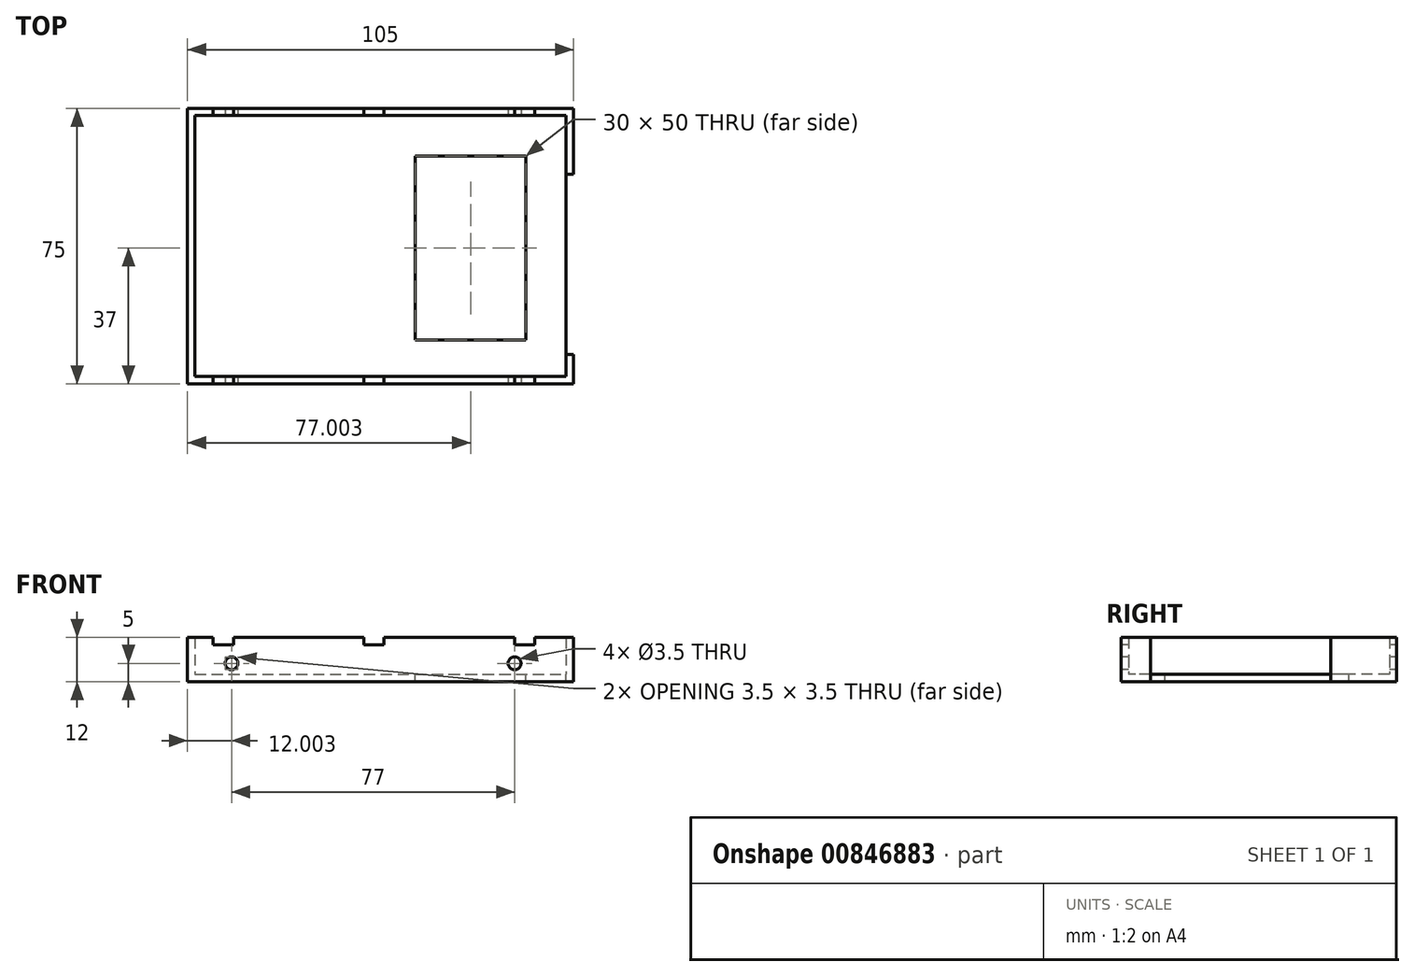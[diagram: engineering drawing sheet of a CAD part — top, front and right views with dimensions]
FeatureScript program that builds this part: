
annotation { "Feature Type Name" : "Feature", "Feature Type Description" : "" }
export const myFeature = defineFeature(function(context is Context, id is Id, definition is map)
    precondition{}
    {
        {
            var Q0;
            Q0=qCreatedBy(makeId("Top.planeOp"),FACE);
            var sketch = newSketch(context, id + "F0", { "sketchPlane" : qUnion([Q0])});
            skLineSegment(sketch, "E0.bottom", {"start": v(-42.38, 29.9) * mm, "end": v(58.62, 29.9) * mm});
            skLineSegment(sketch, "E0.top", {"start": v(-42.38, -41.1) * mm, "end": v(58.62, -41.1) * mm});
            skLineSegment(sketch, "E0.left", {"start": v(-42.38, 29.9) * mm, "end": v(-42.38, -41.1) * mm});
            skLineSegment(sketch, "E0.right", {"start": v(58.62, 29.9) * mm, "end": v(58.62, -41.1) * mm});
            skLineSegment(sketch, "E1.left", {"start": v(-42.38, 29.9) * mm, "end": v(-42.38, 29.9) * mm});
            skLineSegment(sketch, "E1.right", {"start": v(58.62, 29.9) * mm, "end": v(58.62, 29.9) * mm});
            skLineSegment(sketch, "E2.top", {"start": v(-42.38, 31.9) * mm, "end": v(58.62, 31.9) * mm});
            skLineSegment(sketch, "E2.left", {"start": v(-42.38, 29.9) * mm, "end": v(-42.38, 31.9) * mm});
            skLineSegment(sketch, "E2.right", {"start": v(58.62, 29.9) * mm, "end": v(58.62, 31.9) * mm});
            skLineSegment(sketch, "E3.top", {"start": v(-42.38, -43.1) * mm, "end": v(58.62, -43.1) * mm});
            skLineSegment(sketch, "E3.left", {"start": v(-42.38, -41.1) * mm, "end": v(-42.38, -43.1) * mm});
            skLineSegment(sketch, "E3.right", {"start": v(58.62, -41.1) * mm, "end": v(58.62, -43.1) * mm});
            skLineSegment(sketch, "E4.bottom", {"start": v(-42.38, 31.9) * mm, "end": v(-44.38, 31.9) * mm});
            skLineSegment(sketch, "E4.top", {"start": v(-42.38, -43.1) * mm, "end": v(-44.38, -43.1) * mm});
            skLineSegment(sketch, "E4.left", {"start": v(-42.38, 31.9) * mm, "end": v(-42.38, -43.1) * mm});
            skLineSegment(sketch, "E4.right", {"start": v(-44.38, 31.9) * mm, "end": v(-44.38, -43.1) * mm});
            skLineSegment(sketch, "E5.bottom", {"start": v(58.62, 31.9) * mm, "end": v(60.62, 31.9) * mm});
            skLineSegment(sketch, "E5.top", {"start": v(58.62, -43.1) * mm, "end": v(60.62, -43.1) * mm});
            skLineSegment(sketch, "E5.left", {"start": v(58.62, 31.9) * mm, "end": v(58.62, -43.1) * mm});
            skLineSegment(sketch, "E5.right", {"start": v(60.62, 31.9) * mm, "end": v(60.62, -43.1) * mm});
            skSolve(sketch);
        }
        {
            var Q0;
            {var subQ3=sQuery(id+"F0.wireOp",EDGE,"E4.bottom");Q0=makeQuery(id+"F0.imprint","IMPRINT",FACE,{"disambiguationData":[TD([[makeQuery(id+"F0.imprint","IMPRINT",EDGE,{"derivedFrom":subQ3}),1.0]])]});}
            var Q1;
            {var subQ0=sQuery(id+"F0.wireOp",EDGE,"E0.bottom");Q1=makeQuery(id+"F0.imprint","IMPRINT",FACE,{"disambiguationData":[TD([[makeQuery(id+"F0.imprint","IMPRINT",EDGE,{"derivedFrom":subQ0}),1.0]])]});}
            var Q2;
            {var subQ3=sQuery(id+"F0.wireOp",EDGE,"E5.bottom");Q2=makeQuery(id+"F0.imprint","IMPRINT",FACE,{"disambiguationData":[TD([[makeQuery(id+"F0.imprint","IMPRINT",EDGE,{"derivedFrom":subQ3}),-1.0]])]});}
            var Q3;
            {var subQ0=sQuery(id+"F0.wireOp",EDGE,"E0.top");Q3=makeQuery(id+"F0.imprint","IMPRINT",FACE,{"disambiguationData":[TD([[makeQuery(id+"F0.imprint","IMPRINT",EDGE,{"derivedFrom":subQ0}),-1.0]])]});}
            extrude(context, id + "F1", {"entities" : qUnion([Q0, Q1, Q2, Q3]), "depth" : 12 * mm, "offsetDistance" : 25 * mm});
        }
        {
            var Q0;
            {var subQ0=sQuery(id+"F0.wireOp",EDGE,"E0.bottom");Q0=makeQuery(id+"F0.imprint","IMPRINT",FACE,{"disambiguationData":[TD([[makeQuery(id+"F0.imprint","IMPRINT",EDGE,{"derivedFrom":subQ0}),-1.0]])]});}
            extrude(context, id + "F2", {"entities" : qUnion([Q0]), "operationType" : NewBodyOperationType.ADD, "depth" : 2 * mm, "offsetDistance" : 25 * mm});
        }
        {
            var Q0;
            Q0=makeQuery(id+"F1.opExtrude","SWEPT_FACE",FACE,{"disambiguationData":[OSD([sQuery(id+"F0.wireOp",EDGE,"E5.right")])]});
            var sketch = newSketch(context, id + "F3", { "sketchPlane" : qUnion([Q0])});
            skLineSegment(sketch, "E6.bottom", {"start": v(-35.1, 0) * mm, "end": v(13.9, 0) * mm});
            skLineSegment(sketch, "E6.top", {"start": v(-35.1, 12) * mm, "end": v(13.9, 12) * mm});
            skLineSegment(sketch, "E6.left", {"start": v(-35.1, 0) * mm, "end": v(-35.1, 12) * mm});
            skLineSegment(sketch, "E6.right", {"start": v(13.9, 0) * mm, "end": v(13.9, 12) * mm});
            skSolve(sketch);
        }
        {
            var Q0;
            Q0=makeQuery(id+"F1.opExtrude","SWEPT_FACE",FACE,{"disambiguationData":[OSD([sQuery(id+"F0.wireOp",EDGE,"E3.top"),sQuery(id+"F0.wireOp",EDGE,"E4.top"),sQuery(id+"F0.wireOp",EDGE,"E5.top")])]});
            var sketch = newSketch(context, id + "F4", { "sketchPlane" : qUnion([Q0])});
            skCircle(sketch, "E7", {"center": v(44.62, 5) * mm, "radius": 1.75 * mm});
            skCircle(sketch, "E8.1.0.0", {"center": v(-32.38, 5) * mm, "radius": 1.75 * mm});
            skLineSegment(sketch, "E8.direction1", {"start": v(44.62, 5) * mm, "end": v(-32.38, 5) * mm, "construction": true});
            skSolve(sketch);
        }
        {
            var Q0;
            Q0=makeQuery(id+"F4.imprint","IMPRINT",FACE,{"disambiguationData":[TD([[makeQuery(id+"F4.imprint","IMPRINT",EDGE,{"derivedFrom":sQuery(id+"F4.wireOp",EDGE,"E7")}),1.0]])]});
            var Q1;
            Q1=makeQuery(id+"F4.imprint","IMPRINT",FACE,{"disambiguationData":[TD([[makeQuery(id+"F4.imprint","IMPRINT",EDGE,{"derivedFrom":sQuery(id+"F4.wireOp",EDGE,"E8.1.0.0")}),1.0]])]});
            extrude(context, id + "F5", {"entities" : qUnion([Q0, Q1]), "operationType" : NewBodyOperationType.REMOVE, "oppositeDirection" : true, "depth" : 100 * mm, "offsetDistance" : 25 * mm});
        }
        {
            var Q0;
            {var subQ0=sQuery(id+"F3.wireOp",EDGE,"E6.top");Q0=makeQuery(id+"F3.imprint","IMPRINT",FACE,{"disambiguationData":[TD([[makeQuery(id+"F3.imprint","IMPRINT",EDGE,{"derivedFrom":subQ0}),-1.0]])]});}
            var Q1;
            {var subQ0=sQuery(id+"F3.wireOp",EDGE,"E6.bottom");Q1=makeQuery(id+"F3.imprint","IMPRINT",FACE,{"disambiguationData":[TD([[makeQuery(id+"F3.imprint","IMPRINT",EDGE,{"derivedFrom":subQ0}),-1.0]])]});}
            extrude(context, id + "F6", {"entities" : qUnion([Q0, Q1]), "operationType" : NewBodyOperationType.REMOVE, "oppositeDirection" : true, "depth" : 2 * mm, "offsetDistance" : 25 * mm});
        }
        {
            var Q0;
            Q0=makeQuery(id+"F2.opExtrude","CAP_FACE",FACE,{"disambiguationData":[OSD([sQuery(id+"F0.wireOp",EDGE,"E0.bottom"),sQuery(id+"F0.wireOp",EDGE,"E0.top"),sQuery(id+"F0.wireOp",EDGE,"E4.left"),sQuery(id+"F0.wireOp",EDGE,"E5.left")])],"isStart":false});
            var sketch = newSketch(context, id + "F7", { "sketchPlane" : qUnion([Q0])});
            skLineSegment(sketch, "E9.bottom", {"start": v(-32.38, -31.1) * mm, "end": v(47.62, -31.1) * mm});
            skLineSegment(sketch, "E9.top", {"start": v(-32.38, 18.9) * mm, "end": v(47.62, 18.9) * mm});
            skLineSegment(sketch, "E9.left", {"start": v(2.62, -31.1) * mm, "end": v(2.62, 18.9) * mm});
            skLineSegment(sketch, "E9.right", {"start": v(47.62, -31.1) * mm, "end": v(47.62, 18.9) * mm});
            skLineSegment(sketch, "E10.bottom", {"start": v(2.62, 18.9) * mm, "end": v(17.62, 18.9) * mm});
            skLineSegment(sketch, "E10.top", {"start": v(2.62, -31.1) * mm, "end": v(17.62, -31.1) * mm});
            skLineSegment(sketch, "E10.left", {"start": v(2.62, 18.9) * mm, "end": v(2.62, -31.1) * mm});
            skLineSegment(sketch, "E10.right", {"start": v(17.62, 18.9) * mm, "end": v(17.62, -31.1) * mm});
            skLineSegment(sketch, "E11", {"start": v(-32.38, 18.9) * mm, "end": v(-32.38, -31.1) * mm});
            skSolve(sketch);
        }
        {
            var Q0;
            {var subQ2=sQuery(id+"F7.wireOp",EDGE,"E10.left");Q0=makeQuery(id+"F7.imprint","IMPRINT",FACE,{"disambiguationData":[TD([[makeQuery(id+"F7.imprint","IMPRINT",EDGE,{"derivedFrom":subQ2}),-1.0]])]});}
            var Q1;
            {var subQ0=sQuery(id+"F7.wireOp",EDGE,"E9.right");Q1=makeQuery(id+"F7.imprint","IMPRINT",FACE,{"disambiguationData":[TD([[makeQuery(id+"F7.imprint","IMPRINT",EDGE,{"derivedFrom":subQ0}),1.0]])]});}
            extrude(context, id + "F8", {"entities" : qUnion([Q0, Q1]), "operationType" : NewBodyOperationType.REMOVE, "oppositeDirection" : true, "depth" : 2 * mm, "offsetDistance" : 25 * mm});
        }
        {
            var Q0;
            Q0=makeQuery(id+"F4.imprint","IMPRINT",FACE,{"disambiguationData":[TD([[makeQuery(id+"F4.imprint","IMPRINT",EDGE,{"derivedFrom":sQuery(id+"F4.wireOp",EDGE,"E7")}),-1.0]])]});
            var sketch = newSketch(context, id + "F9", { "sketchPlane" : qUnion([Q0])});
            skLineSegment(sketch, "E12.bottom", {"start": v(-37.38, 10) * mm, "end": v(-31.88, 10) * mm});
            skLineSegment(sketch, "E12.top", {"start": v(-37.38, 12) * mm, "end": v(-31.88, 12) * mm});
            skLineSegment(sketch, "E12.left", {"start": v(-37.38, 10) * mm, "end": v(-37.38, 12) * mm});
            skLineSegment(sketch, "E12.right", {"start": v(-31.88, 10) * mm, "end": v(-31.88, 12) * mm});
            skLineSegment(sketch, "E13.1.0.0", {"start": v(3.62, 12) * mm, "end": v(9.12, 12) * mm});
            skLineSegment(sketch, "E13.1.0.1", {"start": v(3.62, 10) * mm, "end": v(9.12, 10) * mm});
            skLineSegment(sketch, "E13.1.0.2", {"start": v(9.12, 10) * mm, "end": v(9.12, 12) * mm});
            skLineSegment(sketch, "E13.1.0.3", {"start": v(3.62, 10) * mm, "end": v(3.62, 12) * mm});
            skLineSegment(sketch, "E13.2.0.0", {"start": v(44.62, 12) * mm, "end": v(50.12, 12) * mm});
            skLineSegment(sketch, "E13.2.0.1", {"start": v(44.62, 10) * mm, "end": v(50.12, 10) * mm});
            skLineSegment(sketch, "E13.2.0.2", {"start": v(50.12, 10) * mm, "end": v(50.12, 12) * mm});
            skLineSegment(sketch, "E13.2.0.3", {"start": v(44.62, 10) * mm, "end": v(44.62, 12) * mm});
            skLineSegment(sketch, "E13.direction1", {"start": v(-37.38, 10) * mm, "end": v(3.62, 10) * mm, "construction": true});
            skSolve(sketch);
        }
        {
            var Q0;
            Q0=makeQuery(id+"F9.imprint","IMPRINT",FACE,{"disambiguationData":[TD([[makeQuery(id+"F9.imprint","IMPRINT",EDGE,{"derivedFrom":sQuery(id+"F9.wireOp",EDGE,"E12.bottom")}),1.0]])]});
            var Q1;
            Q1=makeQuery(id+"F9.imprint","IMPRINT",FACE,{"disambiguationData":[TD([[makeQuery(id+"F9.imprint","IMPRINT",EDGE,{"derivedFrom":sQuery(id+"F9.wireOp",EDGE,"E13.1.0.0")}),1.0]])]});
            var Q2;
            Q2=makeQuery(id+"F9.imprint","IMPRINT",FACE,{"disambiguationData":[TD([[makeQuery(id+"F9.imprint","IMPRINT",EDGE,{"derivedFrom":sQuery(id+"F9.wireOp",EDGE,"E13.2.0.0")}),1.0]])]});
            extrude(context, id + "F10", {"entities" : qUnion([Q0, Q1, Q2]), "operationType" : NewBodyOperationType.REMOVE, "oppositeDirection" : true, "depth" : 80 * mm, "offsetDistance" : 25 * mm});
        }
    });
